# Revit family: TD92_ELE061_BRA010_RVT20_R00
name_source: partatom
category: Mobiliário
units: mm (PartAtom-declared; Revit-internal decimal feet)

## family parameters
Com base no plano de trabalho = Não
Compartilhado = Não
Corte com vazios quando carregada = Não
Número OmniClass = 23.40.20.00
Ponto de cálculo do ambiente = Não
Sempre na vertical = Sim
Título OmniClass = General Furniture and Specialties

## types (1)
- TD92_ELE061_BRA010_RVT20_R00
    Descrição = A Cadeira Tramontina Elena Branca sem Braços em Polipropileno com Pernas Polidas da linha Summa exala elegância com suas formas únicas. É facilmente adaptável com qualquer ambiente interno, resiste a uma carga estática de até 120 kg. Confira também as versões Rodízio, Pé Central e Quatro Pernas.
    Elevação padrão = 0  [stored 0 ft]
    Fabricante = Tramontina Delta S/A
    Modelo = Cadeira Tramontina Elena Branca sem Braços em Polipropileno com Pernas Polidas
    Nota-chave = 92061010
    URL = https://www.tramontinastore.com

note: [stored X ft] marks values corroborated as IEEE doubles in the binary element streams (Revit-internal decimal feet)
